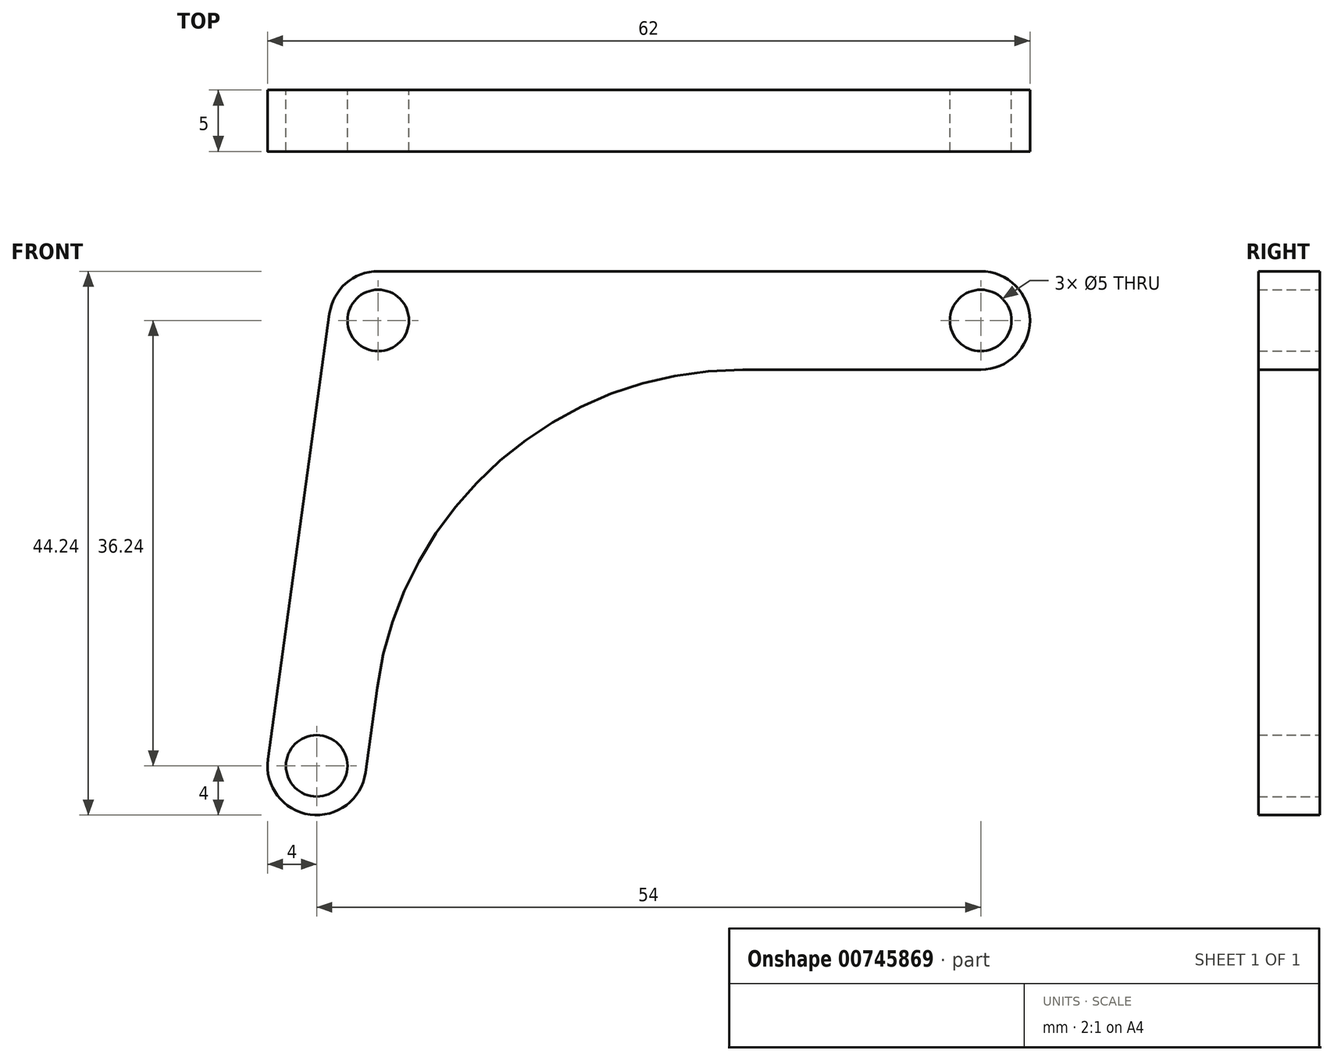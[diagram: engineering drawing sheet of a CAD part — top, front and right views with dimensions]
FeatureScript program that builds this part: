
annotation { "Feature Type Name" : "Feature", "Feature Type Description" : "" }
export const myFeature = defineFeature(function(context is Context, id is Id, definition is map)
    precondition{}
    {
        {
            var Q0;
            Q0=qCreatedBy(makeId("Front.planeOp"),FACE);
            var sketch = newSketch(context, id + "F0", { "sketchPlane" : qUnion([Q0])});
            skArc(sketch, "E0", {"start": v(0, 4) * mm, "mid": v(-2.63, 3.02) * mm, "end": v(-3.96, 0.55) * mm});
            skArc(sketch, "E1", {"start": v(49, -4) * mm, "mid": v(53, 0) * mm, "end": v(49, 4) * mm});
            skArc(sketch, "E2", {"start": v(-8.96, -35.7) * mm, "mid": v(-5.55, -40.2) * mm, "end": v(-1.04, -36.79) * mm});
            skLineSegment(sketch, "E3", {"start": v(0, 4) * mm, "end": v(49, 4) * mm});
            skLineSegment(sketch, "E4", {"start": v(-3.96, 0.55) * mm, "end": v(-8.96, -35.7) * mm});
            skArc(sketch, "E5", {"start": v(29.63, -4) * mm, "mid": v(9.92, -11.38) * mm, "end": v(-0.09, -29.9) * mm});
            skLineSegment(sketch, "E6.trimOffspring", {"start": v(29.63, -4) * mm, "end": v(49, -4) * mm});
            skLineSegment(sketch, "E7.trimOffspring", {"start": v(-0.09, -29.9) * mm, "end": v(-1.04, -36.79) * mm});
            skCircle(sketch, "E8", {"center": v(0, 0) * mm, "radius": 2.5 * mm});
            skCircle(sketch, "E9", {"center": v(-5, -36.24) * mm, "radius": 2.5 * mm});
            skCircle(sketch, "E10", {"center": v(49, 0) * mm, "radius": 2.5 * mm});
            skSolve(sketch);
        }
        {
            var Q0;
            Q0 = qSketchRegion(id + "F0", true);
            extrude(context, id + "F1", {"entities" : qUnion([Q0]), "depth" : 5 * mm, "offsetDistance" : 25.4 * mm});
        }
    });
